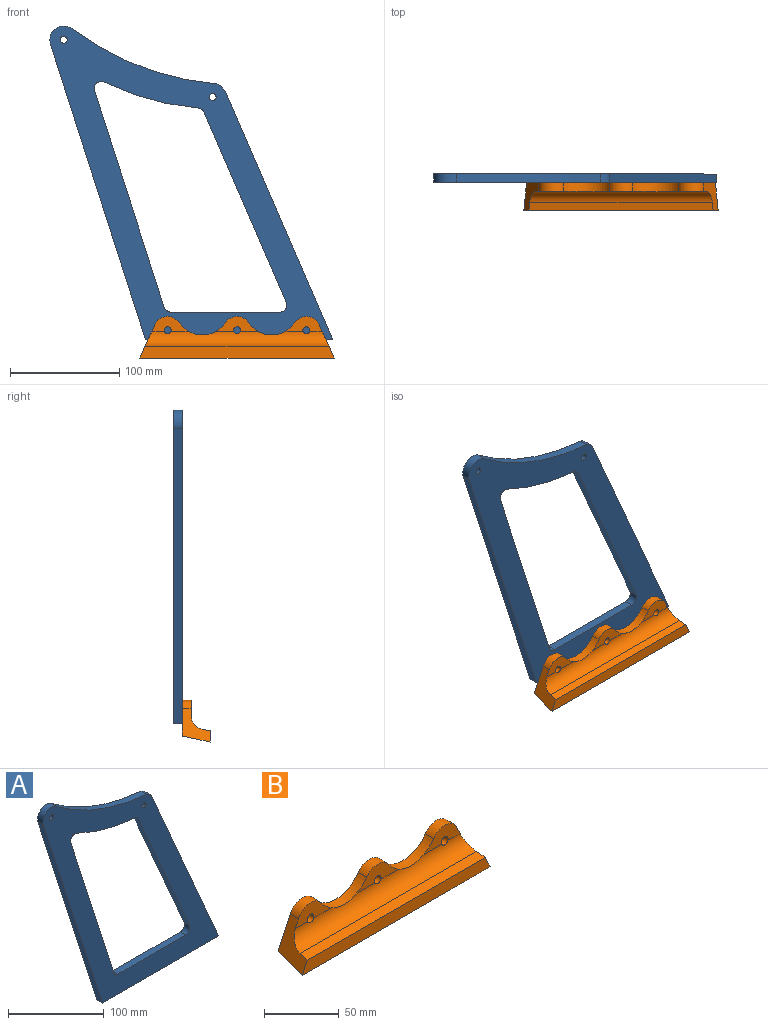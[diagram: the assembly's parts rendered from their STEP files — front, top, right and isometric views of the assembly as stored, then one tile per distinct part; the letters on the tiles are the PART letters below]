
ASSEMBLY  parts=2 mates=1
PART A: 18 faces, bbox 259x7.9x287.3 mm
  f0: plane 270.68x86.92mm, normal (-0.95,0,-0.31), area 2253mm2, adj f1,f15,f16,f17
  f1: plane 171.45x7.92mm, normal (0,0,-1), area 1358.7mm2, adj f0,f2,f16,f17
  f2: plane 227.18x98.31mm, normal (0.92,0,0.4), area 1961.7mm2, adj f1,f3,f16,f17
  f3: cylinder r=12.7mm len=8.06mm, axis (0,1,0), area 88.1mm2, adj f2,f4,f16,f17
  f4: cylinder r=254mm len=132.32mm, axis (0,1,0), area 1137.3mm2, adj f3,f15,f16,f17
  f5: cylinder r=6.35mm len=8.87mm, axis (0,1,0), area 99.6mm2, adj f6,f12,f16,f17
  f6: plane 99.96x7.92mm, normal (0,0,1), area 792.2mm2, adj f5,f7,f16,f17
  f7: cylinder r=6.35mm len=7.92mm, axis (0,1,0), area 63.4mm2, adj f6,f8,f16,f17
  f8: plane 198.4x63.71mm, normal (0.95,0,0.31), area 1651.4mm2, adj f7,f9,f16,f17
  f9: cylinder r=6.35mm len=9.14mm, axis (0,1,0), area 117.6mm2, adj f8,f10,f16,f17
  f10: cylinder r=241.3mm len=86.08mm, axis (0,1,0), area 711.6mm2, adj f9,f11,f16,f17
  f11: cylinder r=6.35mm len=7.92mm, axis (0,1,0), area 54.3mm2, adj f10,f12,f16,f17
  f12: plane 174.09x75.34mm, normal (-0.92,0,-0.4), area 1503.3mm2, adj f5,f11,f16,f17
  f13: cylinder r=3.17mm len=7.92mm, axis (0,1,0), area 158.1mm2, adj f16,f17
  f14: cylinder r=3.17mm len=7.92mm, axis (0,1,0), area 158.1mm2, adj f16,f17
  f15: cylinder r=12.7mm len=20.29mm, axis (0,1,0), area 253.8mm2, adj f0,f4,f16,f17
  f16: plane 287.26x258.98mm, normal (0,-1,0), area 19914.4mm2, adj f0,f1,f2,f3,f4,f5,f6,f7
  f17: plane 287.26x258.98mm, normal (0,1,0), area 19914.4mm2, adj f0,f1,f2,f3,f4,f5,f6,f7
PART B: 18 faces, bbox 177.8x25.4x38.1 mm
  f0: plane 30.63x25.4mm, normal (-0.91,0,0.41), area 444.3mm2, adj f5,f9,f11,f14,f15,f16,f17
  f1: plane 30.63x25.4mm, normal (0.91,0,0.41), area 444.3mm2, adj f5,f10,f11,f12,f14,f16,f17
  f2: cylinder r=3.17mm len=8.07mm, axis (0,1,0), area 158.7mm2, adj f11,f14,f15
  f3: cylinder r=3.17mm len=8.07mm, axis (0,1,0), area 158.7mm2, adj f11,f12,f14
  f4: cylinder r=3.17mm len=8.07mm, axis (0,1,0), area 158.7mm2, adj f11,f13,f14
  f5: plane 177.8x10.16mm, normal (0,-1,0), area 1759.9mm2, adj f0,f1,f16,f17
  f6: cylinder r=25.4mm len=42.33mm, axis (0,1,0), area 401.7mm2, adj f7,f10,f11,f12,f13,f14
  f7: cylinder r=12.7mm len=21.17mm, axis (0,1,0), area 198.3mm2, adj f6,f8,f11,f13
  f8: cylinder r=25.4mm len=42.33mm, axis (0,1,0), area 401.7mm2, adj f7,f9,f11,f13,f14,f15
  f9: cylinder r=12.7mm len=22.16mm, axis (0,1,0), area 214.6mm2, adj f0,f8,f11,f15
  f10: cylinder r=12.7mm len=22.16mm, axis (0,1,0), area 214.6mm2, adj f1,f6,f11,f12
  f11: plane 172.93x32.7mm, normal (0,1,0), area 3824.9mm2, adj f0,f1,f2,f3,f4,f6,f7,f8
  f12: plane 34.09x13.94mm, normal (0,-1,0), area 283.9mm2, adj f1,f3,f6,f10,f14
  f13: plane 39.19x13.94mm, normal (0,-1,0), area 298.2mm2, adj f4,f6,f7,f8,f14
  f14: cylinder r=12.7mm len=167.2mm, axis (-1,0,0), area 2685.3mm2, adj f0,f1,f2,f3,f4,f6,f8,f12
  f15: plane 34.09x13.94mm, normal (0,-1,0), area 283.9mm2, adj f0,f2,f8,f9,f14
  f16: plane 168.63x7.42mm, normal (0,-0.21,0.98), area 1273mm2, adj f0,f1,f5,f14
  f17: plane 177.8x25.4mm, normal (0,0.21,-0.98), area 4553.7mm2, adj f0,f1,f5,f11
PLACE A t=(61.74,61.87,-26.66)mm
PLACE B t=(59.8,53.95,-43.27)mm
MATE planar A.f16 <-> B.f11  axis (0,-1,0) through (-6.87,53.95,3.14)mm
